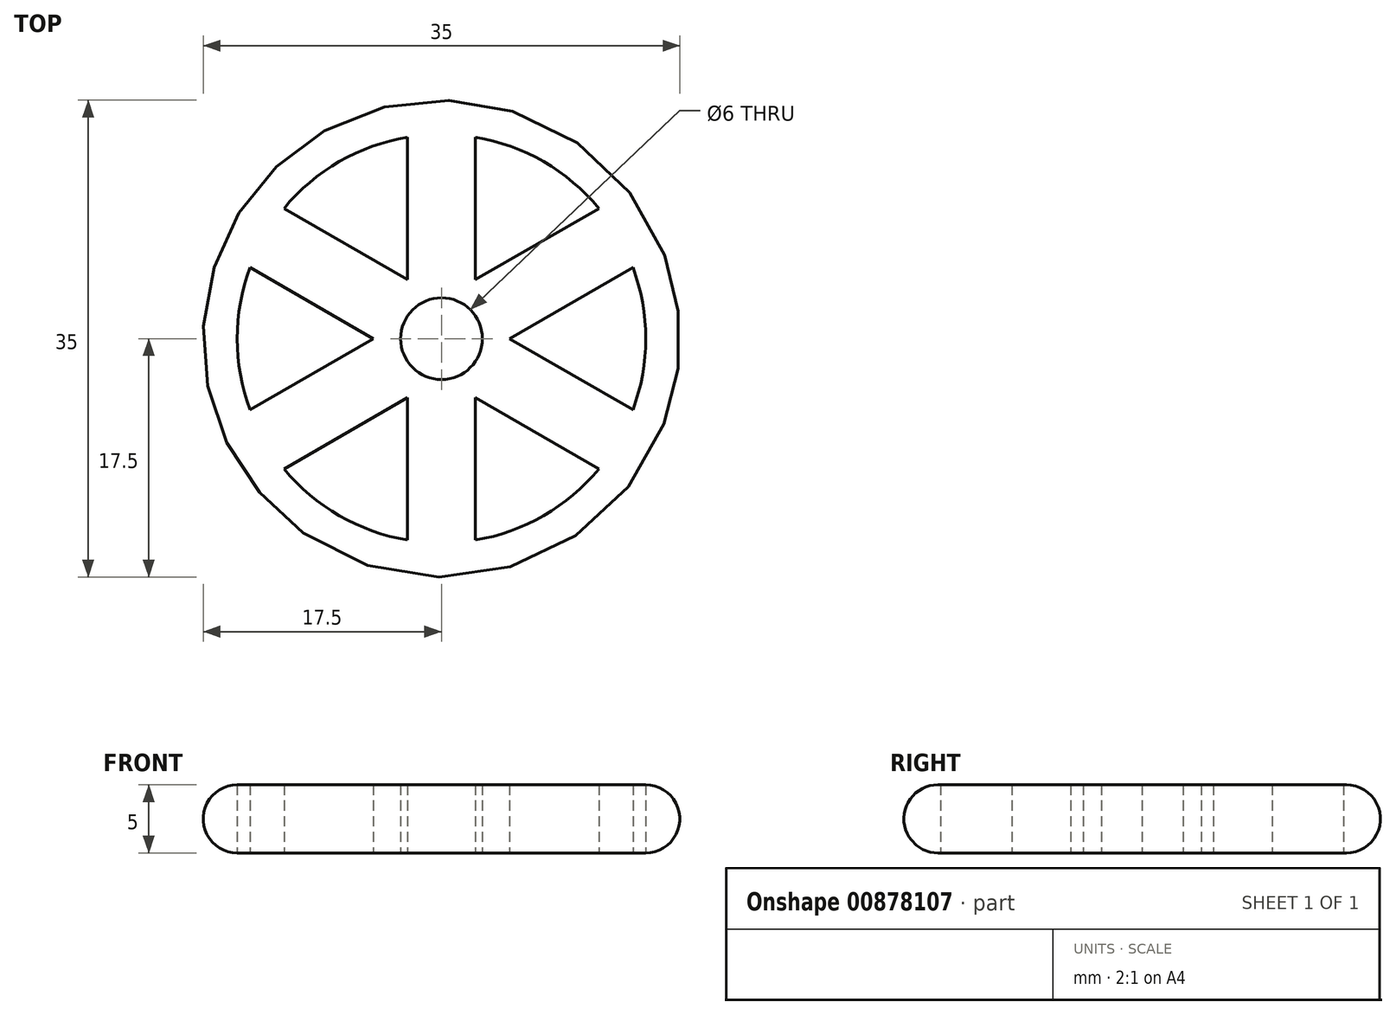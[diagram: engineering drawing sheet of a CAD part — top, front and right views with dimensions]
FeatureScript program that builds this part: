
annotation { "Feature Type Name" : "Feature", "Feature Type Description" : "" }
export const myFeature = defineFeature(function(context is Context, id is Id, definition is map)
    precondition{}
    {
        {
            var Q0;
            Q0=qCreatedBy(makeId("Top.planeOp"),FACE);
            var sketch = newSketch(context, id + "F0", { "sketchPlane" : qUnion([Q0])});
            skCircle(sketch, "E0", {"center": v(0, 0) * mm, "radius": 17.5 * mm});
            skArc(sketch, "E1", {"start": v(-2.5, 14.8) * mm, "mid": v(-7.5, 13) * mm, "end": v(-11.56, 9.56) * mm});
            skLineSegment(sketch, "E2", {"start": v(2.5, 7.5) * mm, "end": v(2.5, 14.8) * mm});
            skLineSegment(sketch, "E3", {"start": v(2.5, 14.8) * mm, "end": v(2.5, 4.33) * mm});
            skLineSegment(sketch, "E4", {"start": v(2.5, 4.33) * mm, "end": v(2.5, 7.5) * mm});
            skLineSegment(sketch, "E5", {"start": v(-2.5, 7.5) * mm, "end": v(-2.5, 14.8) * mm});
            skLineSegment(sketch, "E6", {"start": v(-2.5, 14.8) * mm, "end": v(-2.5, 4.33) * mm});
            skLineSegment(sketch, "E7.1.0", {"start": v(-14.06, 5.23) * mm, "end": v(-5, 0) * mm});
            skLineSegment(sketch, "E7.1.1", {"start": v(-11.56, 9.56) * mm, "end": v(-2.5, 4.33) * mm});
            skLineSegment(sketch, "E7.2.0", {"start": v(-11.56, -9.56) * mm, "end": v(-2.5, -4.33) * mm});
            skLineSegment(sketch, "E7.2.1", {"start": v(-14.06, -5.23) * mm, "end": v(-5, 0) * mm});
            skLineSegment(sketch, "E7.3.0", {"start": v(2.5, -14.8) * mm, "end": v(2.5, -4.33) * mm});
            skLineSegment(sketch, "E7.3.1", {"start": v(-2.5, -14.8) * mm, "end": v(-2.5, -4.33) * mm});
            skLineSegment(sketch, "E7.4.0", {"start": v(14.06, -5.23) * mm, "end": v(5, 0) * mm});
            skLineSegment(sketch, "E7.4.1", {"start": v(11.56, -9.56) * mm, "end": v(2.5, -4.33) * mm});
            skLineSegment(sketch, "E7.5.0", {"start": v(11.56, 9.56) * mm, "end": v(2.5, 4.33) * mm});
            skLineSegment(sketch, "E7.5.1", {"start": v(14.06, 5.23) * mm, "end": v(5, 0) * mm});
            skArc(sketch, "E8.trimOffspring", {"start": v(11.56, 9.56) * mm, "mid": v(7.5, 13) * mm, "end": v(2.5, 14.8) * mm});
            skArc(sketch, "E9.trimOffspring", {"start": v(14.06, -5.23) * mm, "mid": v(15, 0) * mm, "end": v(14.06, 5.23) * mm});
            skArc(sketch, "E10.trimOffspring", {"start": v(2.5, -14.8) * mm, "mid": v(7.5, -13) * mm, "end": v(11.56, -9.56) * mm});
            skArc(sketch, "E11.trimOffspring", {"start": v(-11.56, -9.56) * mm, "mid": v(-7.5, -13) * mm, "end": v(-2.5, -14.8) * mm});
            skArc(sketch, "E12.trimOffspring", {"start": v(-14.06, 5.23) * mm, "mid": v(-15, 0) * mm, "end": v(-14.06, -5.23) * mm});
            skCircle(sketch, "E13", {"center": v(0, 0) * mm, "radius": 3 * mm});
            skSolve(sketch);
        }
        {
            var Q0;
            Q0=makeQuery(id+"F0.imprint","IMPRINT",FACE,{"disambiguationData":[TD([[makeQuery(id+"F0.imprint","IMPRINT",EDGE,{"derivedFrom":sQuery(id+"F0.wireOp",EDGE,"E0")}),1.0]])]});
            extrude(context, id + "F1", {"entities" : qUnion([Q0]), "depth" : 5 * mm, "offsetDistance" : 25 * mm});
        }
        {
            var Q0;
            Q0=makeQuery(id+"F1.opExtrude","CAP_EDGE",EDGE,{"disambiguationData":[OSD([sQuery(id+"F0.wireOp",EDGE,"E0")])],"isStart":false});
            var Q1;
            Q1=makeQuery(id+"F1.opExtrude","CAP_EDGE",EDGE,{"disambiguationData":[OSD([sQuery(id+"F0.wireOp",EDGE,"E0")])],"isStart":true});
            fillet(context, id + "F2", {"entities" : qUnion([Q0, Q1]), "radius" : 2.5 * mm, "tangentPropagation" : true, "allowEdgeOverflow" : false});
        }
    });
